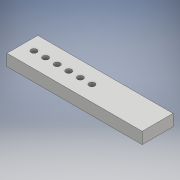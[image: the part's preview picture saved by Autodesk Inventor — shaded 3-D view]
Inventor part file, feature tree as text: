
AUTODESK INVENTOR PART (.ipt)
format: ipt  version: 2017 (Build 210142000, 142)  size: 108,544 bytes
history: native  units: mm
features: sketch x2, extrude x1, hole x1
ambient origin geometry x8: Origin, YZ Plane, XZ Plane, XY Plane, X Axis, Y Axis, Z Axis, Center Point
bodies: Solid1 (feature_tree)
feature tree (4):
  extrude  "Extrusion1"  Depth=8.0mm
  hole  "Hole1"  [1 undecoded]
  sketch  "Sketch1"  dims[d0=35.0mm d1=8.0mm]
  sketch  "Sketch2"  dims[d2=3.0mm d3=0.0mm d4=3.0mm d5=3.0mm d6=3.0mm d7=3.0mm d8=3.0mm d9=3.0mm d10=4.0mm d11=1.5mm d12=6.0mm d13=4.0mm d14=2.0mm d15=90.0deg d16=8.0mm d17=20.594885mm]
note: 1 required parameter value undecoded (feature->parameter linkage not recoverable at this tier; creation-order binding heuristic only, values carry confidence <= 0.55)
